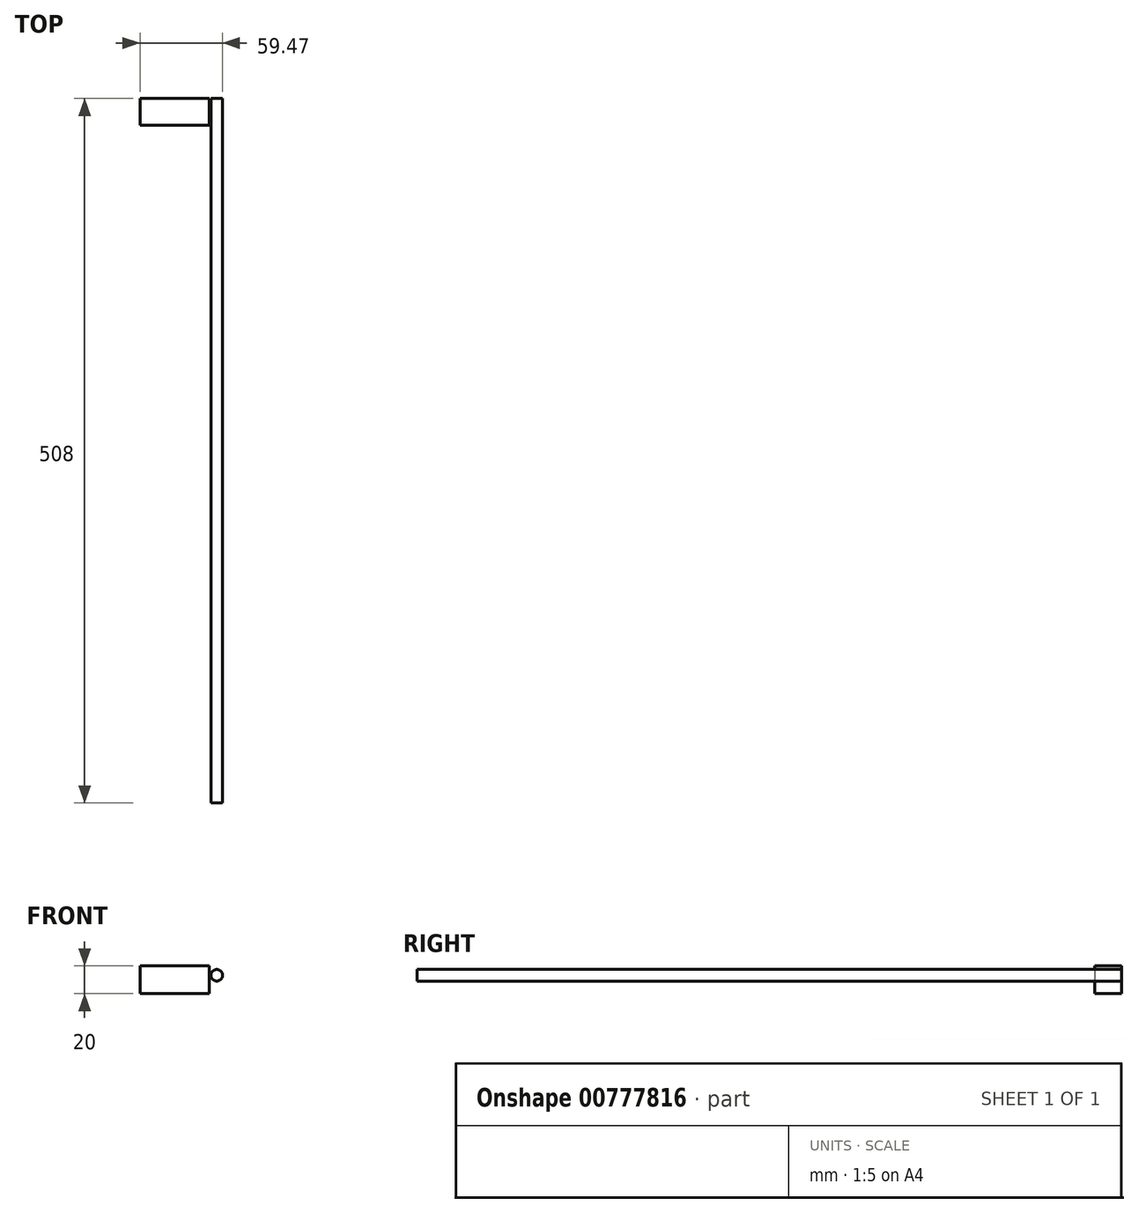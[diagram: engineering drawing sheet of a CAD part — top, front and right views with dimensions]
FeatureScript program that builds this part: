
annotation { "Feature Type Name" : "Feature", "Feature Type Description" : "" }
export const myFeature = defineFeature(function(context is Context, id is Id, definition is map)
    precondition{}
    {
        {
            var Q0;
            Q0=qCreatedBy(makeId("Front.planeOp"),FACE);
            var sketch = newSketch(context, id + "F0", { "sketchPlane" : qUnion([Q0])});
            skLineSegment(sketch, "E0.bottom", {"start": v(-33.52, 10.05) * mm, "end": v(16.48, 10.05) * mm});
            skLineSegment(sketch, "E0.top", {"start": v(-33.52, -9.95) * mm, "end": v(16.48, -9.95) * mm});
            skLineSegment(sketch, "E0.left", {"start": v(-33.52, 10.05) * mm, "end": v(-33.52, -9.95) * mm});
            skLineSegment(sketch, "E0.right", {"start": v(16.48, 10.05) * mm, "end": v(16.48, -9.95) * mm});
            skSolve(sketch);
        }
        {
            var Q0;
            Q0=makeQuery(id+"F0.imprint","IMPRINT",FACE,{"disambiguationData":[TD([[makeQuery(id+"F0.imprint","IMPRINT",EDGE,{"derivedFrom":sQuery(id+"F0.wireOp",EDGE,"E0.bottom")}),-1.0]])]});
            extrude(context, id + "F1", {"entities" : qUnion([Q0]), "depth" : 19.3 * mm, "offsetDistance" : 25.4 * mm});
        }
        {
            var Q0;
            Q0=qCreatedBy(makeId("Front.planeOp"),FACE);
            var sketch = newSketch(context, id + "F2", { "sketchPlane" : qUnion([Q0])});
            skCircle(sketch, "E1", {"center": v(21.78, 3.35) * mm, "radius": 4.17 * mm});
            skSolve(sketch);
        }
        {
            var Q0;
            Q0 = qSketchRegion(id + "F2", true);
            extrude(context, id + "F3", {"entities" : qUnion([Q0]), "depth" : 508 * mm, "offsetDistance" : 25.4 * mm});
        }
    });
